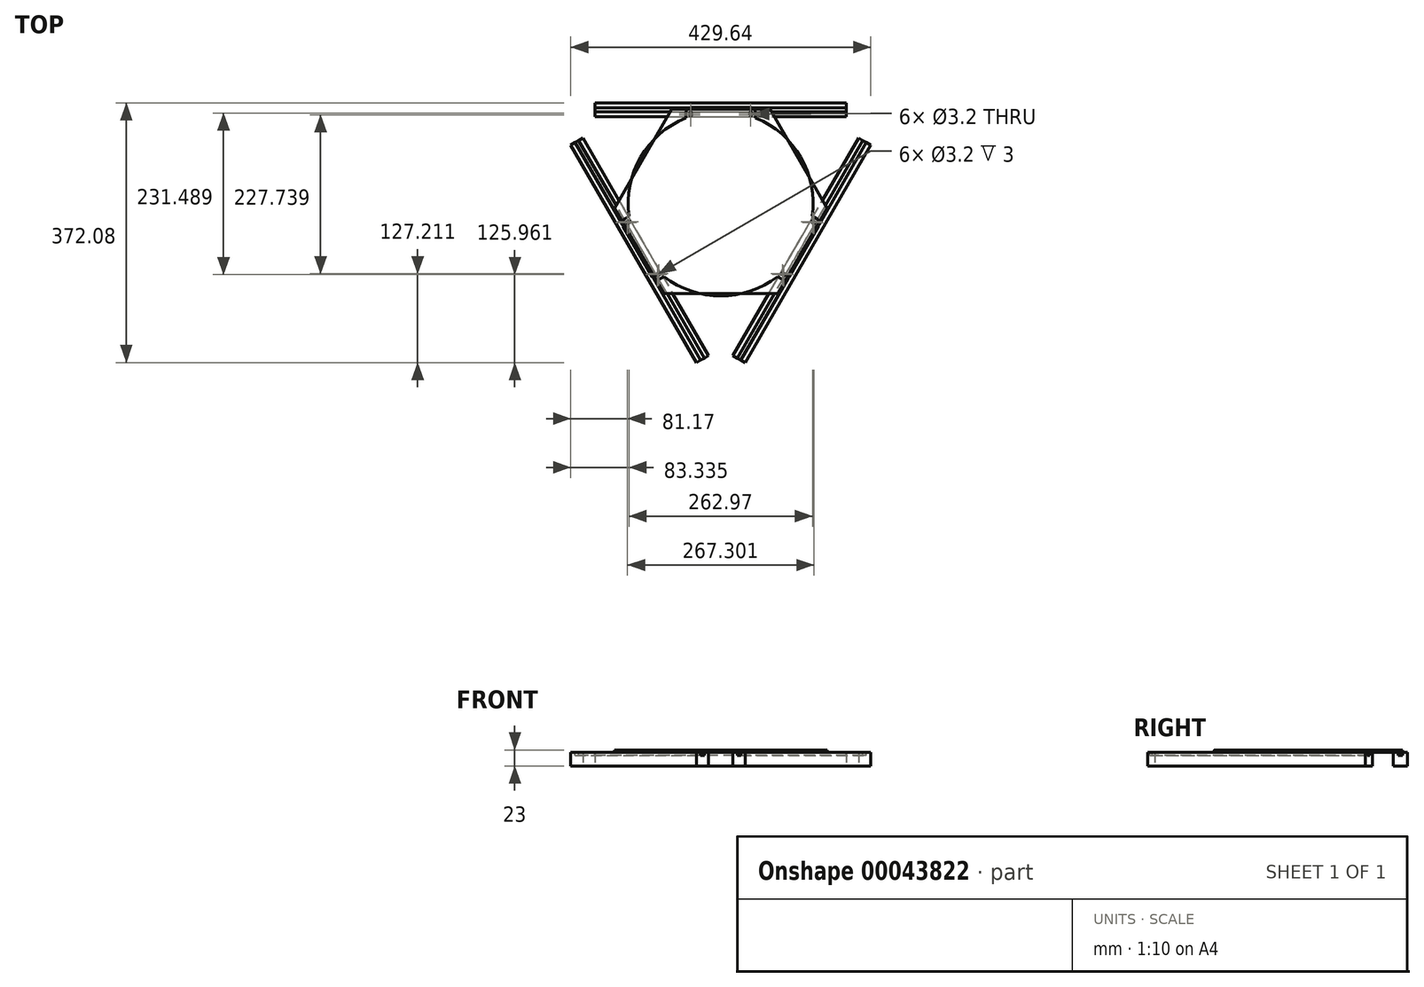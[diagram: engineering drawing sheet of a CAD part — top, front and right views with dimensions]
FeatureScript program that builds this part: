
annotation { "Feature Type Name" : "Feature", "Feature Type Description" : "" }
export const myFeature = defineFeature(function(context is Context, id is Id, definition is map)
    precondition{}
    {
        {
            var Q0;
            Q0=qCreatedBy(makeId("Top.planeOp"),FACE);
            var sketch = newSketch(context, id + "F0", { "sketchPlane" : qUnion([Q0])});
            skLineSegment(sketch, "E0.bottom", {"start": v(0, 0) * mm, "end": v(180, 0) * mm});
            skLineSegment(sketch, "E0.top", {"start": v(0, 20) * mm, "end": v(180, 20) * mm});
            skLineSegment(sketch, "E0.left", {"start": v(0, 0) * mm, "end": v(0, 20) * mm});
            skLineSegment(sketch, "E0.right", {"start": v(180, 0) * mm, "end": v(180, 20) * mm});
            skLineSegment(sketch, "E1.bottom", {"start": v(0, 0) * mm, "end": v(0, 0) * mm});
            skLineSegment(sketch, "E1.top", {"start": v(0, 20) * mm, "end": v(0, 20) * mm});
            skLineSegment(sketch, "E2.bottom", {"start": v(-180, 20) * mm, "end": v(0, 20) * mm});
            skLineSegment(sketch, "E2.top", {"start": v(-180, 0) * mm, "end": v(0, 0) * mm});
            skLineSegment(sketch, "E2.left", {"start": v(-180, 20) * mm, "end": v(-180, 0) * mm});
            skLineSegment(sketch, "E2.right", {"start": v(0, 20) * mm, "end": v(0, 0) * mm});
            skLineSegment(sketch, "E3", {"start": v(-180, 0) * mm, "end": v(-197.5, -30.31) * mm});
            skLineSegment(sketch, "E4.bottom", {"start": v(-197.5, -30.31) * mm, "end": v(-17.5, -342.08) * mm});
            skLineSegment(sketch, "E4.top", {"start": v(-214.82, -40.31) * mm, "end": v(-34.82, -352.08) * mm});
            skLineSegment(sketch, "E4.left", {"start": v(-197.5, -30.31) * mm, "end": v(-214.82, -40.31) * mm});
            skLineSegment(sketch, "E4.right", {"start": v(-17.5, -342.08) * mm, "end": v(-34.82, -352.08) * mm});
            skLineSegment(sketch, "E5", {"start": v(-17.5, -342.08) * mm, "end": v(17.5, -342.08) * mm});
            skLineSegment(sketch, "E6", {"start": v(180, 0) * mm, "end": v(197.5, -30.31) * mm});
            skLineSegment(sketch, "E7", {"start": v(17.5, -342.08) * mm, "end": v(197.5, -30.31) * mm});
            skLineSegment(sketch, "E8", {"start": v(17.5, -342.08) * mm, "end": v(34.82, -352.08) * mm});
            skLineSegment(sketch, "E9", {"start": v(34.82, -352.08) * mm, "end": v(214.82, -40.31) * mm});
            skLineSegment(sketch, "E10", {"start": v(214.82, -40.31) * mm, "end": v(197.5, -30.31) * mm});
            skLineSegment(sketch, "E11", {"start": v(-17.5, -342.08) * mm, "end": v(0, -342.08) * mm});
            skLineSegment(sketch, "E12", {"start": v(0, -342.08) * mm, "end": v(0, 0) * mm});
            skLineSegment(sketch, "E13", {"start": v(197.5, -30.31) * mm, "end": v(188.75, -15.16) * mm});
            skLineSegment(sketch, "E14", {"start": v(-197.5, -30.31) * mm, "end": v(-188.75, -15.16) * mm});
            skLineSegment(sketch, "E15", {"start": v(-197.5, -30.31) * mm, "end": v(-107.5, -186.2) * mm});
            skLineSegment(sketch, "E16", {"start": v(197.5, -30.31) * mm, "end": v(107.5, -186.2) * mm});
            skLineSegment(sketch, "E17", {"start": v(107.5, -186.2) * mm, "end": v(-188.75, -15.16) * mm});
            skLineSegment(sketch, "E18", {"start": v(-107.5, -186.2) * mm, "end": v(188.75, -15.16) * mm});
            skCircle(sketch, "E19", {"center": v(0, -124.13) * mm, "radius": 132.5 * mm});
            skCircle(sketch, "E20", {"center": v(0, -124.13) * mm, "radius": 5 * mm});
            skSolve(sketch);
        }
        {
            var Q0;
            Q0=makeQuery(id+"F0.imprint","IMPRINT",FACE,{"disambiguationData":[TD([[makeQuery(id+"F0.imprint","IMPRINT",EDGE,{"derivedFrom":sQuery(id+"F0.wireOp",EDGE,"E0.bottom")}),1.0]])]});
            var Q1;
            Q1=makeQuery(id+"F0.imprint","IMPRINT",FACE,{"disambiguationData":[TD([[makeQuery(id+"F0.imprint","IMPRINT",EDGE,{"derivedFrom":sQuery(id+"F0.wireOp",EDGE,"E2.bottom")}),-1.0]])]});
            var Q2;
            Q2=makeQuery(id+"F0.imprint","IMPRINT",FACE,{"disambiguationData":[TD([[makeQuery(id+"F0.imprint","IMPRINT",EDGE,{"derivedFrom":sQuery(id+"F0.wireOp",EDGE,"E4.bottom")}),-1.0]])]});
            var Q3;
            Q3=makeQuery(id+"F0.imprint","IMPRINT",FACE,{"disambiguationData":[TD([[makeQuery(id+"F0.imprint","IMPRINT",EDGE,{"derivedFrom":sQuery(id+"F0.wireOp",EDGE,"E7")}),-1.0]])]});
            var Q4;
            {var subQ1=sQuery(id+"F0.wireOp",EDGE,"E0.top");Q4=makeQuery(id+"F0.imprint","IMPRINT",FACE,{"disambiguationData":[TD([[makeQuery(id+"F0.imprint","IMPRINT",EDGE,{"derivedFrom":subQ1}),-1.0]])]});}
            var Q5;
            {var subQ1=sQuery(id+"F0.wireOp",EDGE,"E2.top");var subQ3=sQuery(id+"F0.wireOp",EDGE,"E19");var subQ4=makeQuery(id+"F0.imprint","INTERSECT",VERTEX,{"derivedFrom":[subQ1,subQ3]});Q5=makeQuery(id+"F0.imprint","IMPRINT",FACE,{"disambiguationData":[TD([[makeQuery(id+"F0.imprint","IMPRINT",EDGE,{"disambiguationData":[TD([[subQ4,1.0]])],"derivedFrom":subQ3}),1.0]])]});}
            var Q6;
            {var subQ1=sQuery(id+"F0.wireOp",EDGE,"E8");Q6=makeQuery(id+"F0.imprint","IMPRINT",FACE,{"disambiguationData":[TD([[makeQuery(id+"F0.imprint","IMPRINT",EDGE,{"derivedFrom":subQ1}),1.0]])]});}
            var Q7;
            Q7=makeQuery(id+"F0.imprint","IMPRINT",FACE,{"disambiguationData":[TD([[makeQuery(id+"F0.imprint","IMPRINT",EDGE,{"derivedFrom":sQuery(id+"F0.wireOp",EDGE,"E4.top")}),1.0]])]});
            extrude(context, id + "F1", {"entities" : qUnion([Q0, Q1, Q2, Q3, Q4, Q5, Q6, Q7]), "depth" : 20 * mm});
        }
        {
            var Q0;
            {var subQ1=sQuery(id+"F0.wireOp",EDGE,"E15");var subQ3=sQuery(id+"F0.wireOp",EDGE,"E19");var subQ4=makeQuery(id+"F0.imprint","INTERSECT",VERTEX,{"derivedFrom":[subQ1,subQ3]});Q0=makeQuery(id+"F0.imprint","IMPRINT",FACE,{"disambiguationData":[TD([[makeQuery(id+"F0.imprint","IMPRINT",EDGE,{"disambiguationData":[TD([[subQ4,1.0]])],"derivedFrom":subQ3}),1.0]])]});}
            var Q1;
            {var subQ1=sQuery(id+"F0.wireOp",EDGE,"E2.top");var subQ3=sQuery(id+"F0.wireOp",EDGE,"E19");var subQ4=makeQuery(id+"F0.imprint","INTERSECT",VERTEX,{"derivedFrom":[subQ1,subQ3]});Q1=makeQuery(id+"F0.imprint","IMPRINT",FACE,{"disambiguationData":[TD([[makeQuery(id+"F0.imprint","IMPRINT",EDGE,{"disambiguationData":[TD([[subQ4,-1.0]])],"derivedFrom":subQ3}),1.0]])]});}
            var Q2;
            {var subQ1=sQuery(id+"F0.wireOp",EDGE,"E0.bottom");var subQ3=sQuery(id+"F0.wireOp",EDGE,"E19");var subQ4=makeQuery(id+"F0.imprint","INTERSECT",VERTEX,{"derivedFrom":[subQ1,subQ3]});Q2=makeQuery(id+"F0.imprint","IMPRINT",FACE,{"disambiguationData":[TD([[makeQuery(id+"F0.imprint","IMPRINT",EDGE,{"disambiguationData":[TD([[subQ4,1.0]])],"derivedFrom":subQ3}),1.0]])]});}
            var Q3;
            {var subQ1=sQuery(id+"F0.wireOp",EDGE,"E16");var subQ3=sQuery(id+"F0.wireOp",EDGE,"E19");var subQ4=makeQuery(id+"F0.imprint","INTERSECT",VERTEX,{"derivedFrom":[subQ1,subQ3]});Q3=makeQuery(id+"F0.imprint","IMPRINT",FACE,{"disambiguationData":[TD([[makeQuery(id+"F0.imprint","IMPRINT",EDGE,{"disambiguationData":[TD([[subQ4,-1.0]])],"derivedFrom":subQ3}),1.0]])]});}
            var Q4;
            {var subQ1=sQuery(id+"F0.wireOp",EDGE,"E7");var subQ3=sQuery(id+"F0.wireOp",EDGE,"E19");var subQ4=makeQuery(id+"F0.imprint","INTERSECT",VERTEX,{"derivedFrom":[subQ1,subQ3]});Q4=makeQuery(id+"F0.imprint","IMPRINT",FACE,{"disambiguationData":[TD([[makeQuery(id+"F0.imprint","IMPRINT",EDGE,{"disambiguationData":[TD([[subQ4,1.0]])],"derivedFrom":subQ3}),1.0]])]});}
            var Q5;
            {var subQ1=sQuery(id+"F0.wireOp",EDGE,"E2.top");var subQ3=sQuery(id+"F0.wireOp",EDGE,"E19");var subQ4=makeQuery(id+"F0.imprint","INTERSECT",VERTEX,{"derivedFrom":[subQ1,subQ3]});Q5=makeQuery(id+"F0.imprint","IMPRINT",FACE,{"disambiguationData":[TD([[makeQuery(id+"F0.imprint","IMPRINT",EDGE,{"disambiguationData":[TD([[subQ4,1.0]])],"derivedFrom":subQ3}),1.0]])]});}
            var Q6;
            {var subQ1=sQuery(id+"F0.wireOp",EDGE,"E0.bottom");var subQ3=sQuery(id+"F0.wireOp",EDGE,"E19");var subQ4=makeQuery(id+"F0.imprint","INTERSECT",VERTEX,{"derivedFrom":[subQ1,subQ3]});Q6=makeQuery(id+"F0.imprint","IMPRINT",FACE,{"disambiguationData":[TD([[makeQuery(id+"F0.imprint","IMPRINT",EDGE,{"disambiguationData":[TD([[subQ4,-1.0]])],"derivedFrom":subQ3}),1.0]])]});}
            var Q7;
            {var subQ1=sQuery(id+"F0.wireOp",EDGE,"E7");var subQ3=sQuery(id+"F0.wireOp",EDGE,"E19");var subQ4=makeQuery(id+"F0.imprint","INTERSECT",VERTEX,{"derivedFrom":[subQ1,subQ3]});Q7=makeQuery(id+"F0.imprint","IMPRINT",FACE,{"disambiguationData":[TD([[makeQuery(id+"F0.imprint","IMPRINT",EDGE,{"disambiguationData":[TD([[subQ4,-1.0]])],"derivedFrom":subQ3}),1.0]])]});}
            var Q8;
            {var subQ1=sQuery(id+"F0.wireOp",EDGE,"E4.bottom");var subQ3=sQuery(id+"F0.wireOp",EDGE,"E19");var subQ4=makeQuery(id+"F0.imprint","INTERSECT",VERTEX,{"derivedFrom":[subQ1,subQ3]});Q8=makeQuery(id+"F0.imprint","IMPRINT",FACE,{"disambiguationData":[TD([[makeQuery(id+"F0.imprint","IMPRINT",EDGE,{"disambiguationData":[TD([[subQ4,1.0]])],"derivedFrom":subQ3}),1.0]])]});}
            var Q9;
            {var subQ1=sQuery(id+"F0.wireOp",EDGE,"E4.bottom");var subQ3=sQuery(id+"F0.wireOp",EDGE,"E19");var subQ4=makeQuery(id+"F0.imprint","INTERSECT",VERTEX,{"derivedFrom":[subQ1,subQ3]});Q9=makeQuery(id+"F0.imprint","IMPRINT",FACE,{"disambiguationData":[TD([[makeQuery(id+"F0.imprint","IMPRINT",EDGE,{"disambiguationData":[TD([[subQ4,-1.0]])],"derivedFrom":subQ3}),1.0]])]});}
            var Q10;
            {var subQ0=sQuery(id+"F0.wireOp",EDGE,"E20");var subQ1=sQuery(id+"F0.wireOp",EDGE,"E12");var subQ2=makeQuery(id+"F0.imprint","INTERSECT",VERTEX,{"disambiguationData":[OD(0.0)],"derivedFrom":[subQ1,subQ0]});Q10=makeQuery(id+"F0.imprint","IMPRINT",FACE,{"disambiguationData":[TD([[makeQuery(id+"F0.imprint","IMPRINT",EDGE,{"disambiguationData":[TD([[subQ2,1.0]])],"derivedFrom":subQ0}),1.0]])]});}
            var Q11;
            {var subQ0=sQuery(id+"F0.wireOp",EDGE,"E20");var subQ1=sQuery(id+"F0.wireOp",EDGE,"E17");var subQ2=makeQuery(id+"F0.imprint","INTERSECT",VERTEX,{"disambiguationData":[OD(1.0)],"derivedFrom":[subQ1,subQ0]});Q11=makeQuery(id+"F0.imprint","IMPRINT",FACE,{"disambiguationData":[TD([[makeQuery(id+"F0.imprint","IMPRINT",EDGE,{"disambiguationData":[TD([[subQ2,-1.0]])],"derivedFrom":subQ0}),1.0]])]});}
            var Q12;
            {var subQ0=sQuery(id+"F0.wireOp",EDGE,"E20");var subQ1=sQuery(id+"F0.wireOp",EDGE,"E12");var subQ2=makeQuery(id+"F0.imprint","INTERSECT",VERTEX,{"disambiguationData":[OD(0.0)],"derivedFrom":[subQ1,subQ0]});Q12=makeQuery(id+"F0.imprint","IMPRINT",FACE,{"disambiguationData":[TD([[makeQuery(id+"F0.imprint","IMPRINT",EDGE,{"disambiguationData":[TD([[subQ2,-1.0]])],"derivedFrom":subQ0}),1.0]])]});}
            var Q13;
            {var subQ0=sQuery(id+"F0.wireOp",EDGE,"E20");var subQ1=sQuery(id+"F0.wireOp",EDGE,"E17");var subQ2=makeQuery(id+"F0.imprint","INTERSECT",VERTEX,{"disambiguationData":[OD(0.0)],"derivedFrom":[subQ1,subQ0]});Q13=makeQuery(id+"F0.imprint","IMPRINT",FACE,{"disambiguationData":[TD([[makeQuery(id+"F0.imprint","IMPRINT",EDGE,{"disambiguationData":[TD([[subQ2,-1.0]])],"derivedFrom":subQ0}),1.0]])]});}
            var Q14;
            {var subQ0=sQuery(id+"F0.wireOp",EDGE,"E20");var subQ1=sQuery(id+"F0.wireOp",EDGE,"E12");var subQ2=makeQuery(id+"F0.imprint","INTERSECT",VERTEX,{"disambiguationData":[OD(1.0)],"derivedFrom":[subQ1,subQ0]});Q14=makeQuery(id+"F0.imprint","IMPRINT",FACE,{"disambiguationData":[TD([[makeQuery(id+"F0.imprint","IMPRINT",EDGE,{"disambiguationData":[TD([[subQ2,1.0]])],"derivedFrom":subQ0}),1.0]])]});}
            var Q15;
            {var subQ0=sQuery(id+"F0.wireOp",EDGE,"E20");var subQ1=sQuery(id+"F0.wireOp",EDGE,"E12");var subQ2=makeQuery(id+"F0.imprint","INTERSECT",VERTEX,{"disambiguationData":[OD(1.0)],"derivedFrom":[subQ1,subQ0]});Q15=makeQuery(id+"F0.imprint","IMPRINT",FACE,{"disambiguationData":[TD([[makeQuery(id+"F0.imprint","IMPRINT",EDGE,{"disambiguationData":[TD([[subQ2,-1.0]])],"derivedFrom":subQ0}),1.0]])]});}
            extrude(context, id + "F2", {"entities" : qUnion([Q0, Q1, Q2, Q3, Q4, Q5, Q6, Q7, Q8, Q9, Q10, Q11, Q12, Q13, Q14, Q15]), "depth" : 23 * mm, "hasSecondDirection" : true, "secondDirectionOppositeDirection" : false, "secondDirectionDepth" : 20 * mm});
        }
        {
            var Q0;
            Q0=makeQuery(id+"F2.opExtrude","CAP_FACE",FACE,{"disambiguationData":[OSD([sQuery(id+"F0.wireOp",EDGE,"E19")])],"isStart":false});
            var sketch = newSketch(context, id + "F3", { "sketchPlane" : qUnion([Q0])});
            skCircle(sketch, "E21", {"center": v(0, -124.13) * mm, "radius": 132.5 * mm});
            skLineSegment(sketch, "E22", {"start": v(0, -124.13) * mm, "end": v(0, 8.37) * mm});
            skLineSegment(sketch, "E23", {"start": v(0, 8.37) * mm, "end": v(0, 13.37) * mm});
            skLineSegment(sketch, "E24", {"start": v(0, 13.37) * mm, "end": v(42, 13.37) * mm});
            skLineSegment(sketch, "E25", {"start": v(50, 5.37) * mm, "end": v(50, -1.43) * mm});
            skCircle(sketch, "E26", {"center": v(43, 5.37) * mm, "radius": 1.6 * mm});
            skPoint(sketch, "E27.visualSharp", {"position": v(50, 13.37) * mm});
            skArc(sketch, "E27.filletArc", {"start": v(50, 5.37) * mm, "mid": v(47.66, 11.03) * mm, "end": v(42, 13.37) * mm});
            skLineSegment(sketch, "E28", {"start": v(0, 13.37) * mm, "end": v(-42, 13.37) * mm});
            skLineSegment(sketch, "E29", {"start": v(-50, 5.37) * mm, "end": v(-50, -1.43) * mm});
            skCircle(sketch, "E30", {"center": v(-43, 5.37) * mm, "radius": 1.6 * mm});
            skPoint(sketch, "E31.visualSharp", {"position": v(-50, 13.37) * mm});
            skArc(sketch, "E31.filletArc", {"start": v(-42, 13.37) * mm, "mid": v(-47.66, 11.03) * mm, "end": v(-50, 5.37) * mm});
            skLineSegment(sketch, "E32.1.0", {"start": v(87.15, -232.18) * mm, "end": v(81.26, -228.78) * mm});
            skArc(sketch, "E32.1.1", {"start": v(87.15, -232.18) * mm, "mid": v(93.22, -232.98) * mm, "end": v(98.08, -229.25) * mm});
            skCircle(sketch, "E32.1.2", {"center": v(90.65, -226.12) * mm, "radius": 1.6 * mm});
            skLineSegment(sketch, "E32.1.3", {"start": v(119.08, -192.88) * mm, "end": v(98.08, -229.25) * mm});
            skLineSegment(sketch, "E32.1.4", {"start": v(119.08, -192.88) * mm, "end": v(140.08, -156.5) * mm});
            skArc(sketch, "E32.1.5", {"start": v(140.08, -156.5) * mm, "mid": v(140.88, -150.44) * mm, "end": v(137.15, -145.58) * mm});
            skLineSegment(sketch, "E32.1.6", {"start": v(137.15, -145.58) * mm, "end": v(131.26, -142.18) * mm});
            skCircle(sketch, "E32.1.7", {"center": v(133.65, -151.64) * mm, "radius": 1.6 * mm});
            skLineSegment(sketch, "E32.2.0", {"start": v(-137.15, -145.58) * mm, "end": v(-131.26, -142.18) * mm});
            skArc(sketch, "E32.2.1", {"start": v(-137.15, -145.58) * mm, "mid": v(-140.88, -150.44) * mm, "end": v(-140.08, -156.5) * mm});
            skCircle(sketch, "E32.2.2", {"center": v(-133.65, -151.64) * mm, "radius": 1.6 * mm});
            skLineSegment(sketch, "E32.2.3", {"start": v(-119.08, -192.88) * mm, "end": v(-140.08, -156.5) * mm});
            skLineSegment(sketch, "E32.2.4", {"start": v(-119.08, -192.88) * mm, "end": v(-98.08, -229.25) * mm});
            skArc(sketch, "E32.2.5", {"start": v(-98.08, -229.25) * mm, "mid": v(-93.22, -232.98) * mm, "end": v(-87.15, -232.18) * mm});
            skLineSegment(sketch, "E32.2.6", {"start": v(-87.15, -232.18) * mm, "end": v(-81.26, -228.78) * mm});
            skCircle(sketch, "E32.2.7", {"center": v(-90.65, -226.12) * mm, "radius": 1.6 * mm});
            skLineSegment(sketch, "E32.anchor1", {"start": v(0, -124.13) * mm, "end": v(50, -1.43) * mm, "construction": true});
            skLineSegment(sketch, "E32.anchor2", {"start": v(0, -124.13) * mm, "end": v(-131.26, -142.18) * mm, "construction": true});
            skSolve(sketch);
        }
        {
            var Q0;
            {var subQ1=sQuery(id+"F3.wireOp",EDGE,"E23");Q0=makeQuery(id+"F3.imprint","IMPRINT",FACE,{"disambiguationData":[TD([[makeQuery(id+"F3.imprint","IMPRINT",EDGE,{"derivedFrom":subQ1}),-1.0]])]});}
            var Q1;
            {var subQ1=sQuery(id+"F3.wireOp",EDGE,"E23");Q1=makeQuery(id+"F3.imprint","IMPRINT",FACE,{"disambiguationData":[TD([[makeQuery(id+"F3.imprint","IMPRINT",EDGE,{"derivedFrom":subQ1}),1.0]])]});}
            var Q2;
            {var subQ0=sQuery(id+"F3.wireOp",EDGE,"E21");var subQ1=makeQuery(id+"F3.imprint","INTERSECT",VERTEX,{"derivedFrom":[subQ0,sQuery(id+"F3.wireOp",EDGE,"E23")]});Q2=makeQuery(id+"F3.imprint","IMPRINT",FACE,{"disambiguationData":[TD([[makeQuery(id+"F3.imprint","IMPRINT",EDGE,{"disambiguationData":[TD([[subQ1,1.0]])],"derivedFrom":subQ0}),1.0]])]});}
            var Q3;
            {var subQ0=sQuery(id+"F3.wireOp",EDGE,"E32.1.0");Q3=makeQuery(id+"F3.imprint","IMPRINT",FACE,{"disambiguationData":[TD([[makeQuery(id+"F3.imprint","IMPRINT",EDGE,{"derivedFrom":subQ0}),-1.0]])]});}
            var Q4;
            {var subQ0=sQuery(id+"F3.wireOp",EDGE,"E32.2.0");Q4=makeQuery(id+"F3.imprint","IMPRINT",FACE,{"disambiguationData":[TD([[makeQuery(id+"F3.imprint","IMPRINT",EDGE,{"derivedFrom":subQ0}),-1.0]])]});}
            extrude(context, id + "F4", {"entities" : qUnion([Q0, Q1, Q2, Q3, Q4]), "operationType" : NewBodyOperationType.ADD, "oppositeDirection" : true, "depth" : 3 * mm});
        }
        {
            var Q0;
            Q0=makeQuery(id+"F1.opExtrude","CAP_FACE",FACE,{"disambiguationData":[OSD([sQuery(id+"F0.wireOp",EDGE,"E0.bottom"),sQuery(id+"F0.wireOp",EDGE,"E0.top"),sQuery(id+"F0.wireOp",EDGE,"E0.right"),sQuery(id+"F0.wireOp",EDGE,"E2.bottom"),sQuery(id+"F0.wireOp",EDGE,"E2.top"),sQuery(id+"F0.wireOp",EDGE,"E2.left")])],"isStart":false});
            var sketch = newSketch(context, id + "F5", { "sketchPlane" : qUnion([Q0])});
            skLineSegment(sketch, "E33.bottom", {"start": v(-180, 10) * mm, "end": v(180, 10) * mm});
            skLineSegment(sketch, "E33.top", {"start": v(-180, 7) * mm, "end": v(180, 7) * mm});
            skLineSegment(sketch, "E33.left", {"start": v(-180, 10) * mm, "end": v(-180, 7) * mm});
            skLineSegment(sketch, "E33.right", {"start": v(180, 10) * mm, "end": v(180, 7) * mm});
            skLineSegment(sketch, "E34.bottom", {"start": v(180, 10) * mm, "end": v(-180, 10) * mm});
            skLineSegment(sketch, "E34.top", {"start": v(180, 13) * mm, "end": v(-180, 13) * mm});
            skLineSegment(sketch, "E34.left", {"start": v(180, 10) * mm, "end": v(180, 13) * mm});
            skLineSegment(sketch, "E34.right", {"start": v(-180, 10) * mm, "end": v(-180, 13) * mm});
            skSolve(sketch);
        }
        {
            var Q0;
            Q0 = qSketchRegion(id + "F5", true);
            extrude(context, id + "F6", {"entities" : qUnion([Q0]), "oppositeDirection" : true, "depth" : 5 * mm});
        }
        {
            var Q0;
            Q0=makeQuery(id+"F6.opExtrude","SWEPT_BODY",BODY,{"disambiguationData":[OSD([sQuery(id+"F5.wireOp",EDGE,"E33.top"),sQuery(id+"F5.wireOp",EDGE,"E33.left"),sQuery(id+"F5.wireOp",EDGE,"E33.right"),sQuery(id+"F5.wireOp",EDGE,"E34.top"),sQuery(id+"F5.wireOp",EDGE,"E34.left"),sQuery(id+"F5.wireOp",EDGE,"E34.right")])]});
            var Q1;
            Q1=sQuery(id+"F0.wireOp",EDGE,"E20");
            circularPattern(context, id + "F7", {"operationType" : NewBodyOperationType.REMOVE, "entities" : qUnion([Q0]), "axis" : qUnion([Q1]), "angle" : 360 * degree, "instanceCount" : 3, "equalSpace" : true});
        }
        {
            var Q0;
            Q0=makeQuery(id+"F2.opExtrude","CAP_FACE",FACE,{"disambiguationData":[OSD([sQuery(id+"F0.wireOp",EDGE,"E19")])],"isStart":false});
            var sketch = newSketch(context, id + "F8", { "sketchPlane" : qUnion([Q0])});
            skLineSegment(sketch, "E35", {"start": v(0, -124.13) * mm, "end": v(0, 10.87) * mm});
            skLineSegment(sketch, "E36", {"start": v(0, 10.87) * mm, "end": v(70.5, 10.87) * mm});
            skLineSegment(sketch, "E37", {"start": v(0, 10.87) * mm, "end": v(-70.5, 10.87) * mm});
            skLineSegment(sketch, "E38", {"start": v(70.5, 10.87) * mm, "end": v(152.5, -131.16) * mm});
            skLineSegment(sketch, "E39", {"start": v(-70.5, 10.87) * mm, "end": v(-152.5, -131.16) * mm});
            skLineSegment(sketch, "E40", {"start": v(-152.5, -131.16) * mm, "end": v(-82, -253.27) * mm});
            skLineSegment(sketch, "E41", {"start": v(152.5, -131.16) * mm, "end": v(82, -253.27) * mm});
            skLineSegment(sketch, "E42", {"start": v(-82, -253.27) * mm, "end": v(82, -253.27) * mm});
            skCircle(sketch, "E43", {"center": v(-43, 2.87) * mm, "radius": 1.6 * mm});
            skCircle(sketch, "E44", {"center": v(43, 2.87) * mm, "radius": 1.6 * mm});
            skCircle(sketch, "E45.1.0", {"center": v(-88.49, -224.87) * mm, "radius": 1.6 * mm});
            skCircle(sketch, "E45.1.1", {"center": v(-131.49, -150.4) * mm, "radius": 1.6 * mm});
            skCircle(sketch, "E45.2.0", {"center": v(131.49, -150.4) * mm, "radius": 1.6 * mm});
            skCircle(sketch, "E45.2.1", {"center": v(88.49, -224.87) * mm, "radius": 1.6 * mm});
            skPoint(sketch, "E45.center", {"position": v(0, -124.13) * mm});
            skSolve(sketch);
        }
        {
            var Q0;
            Q0 = qSketchRegion(id + "F8", true);
            extrude(context, id + "F9", {"entities" : qUnion([Q0]), "oppositeDirection" : true, "depth" : 3 * mm});
        }
    });
